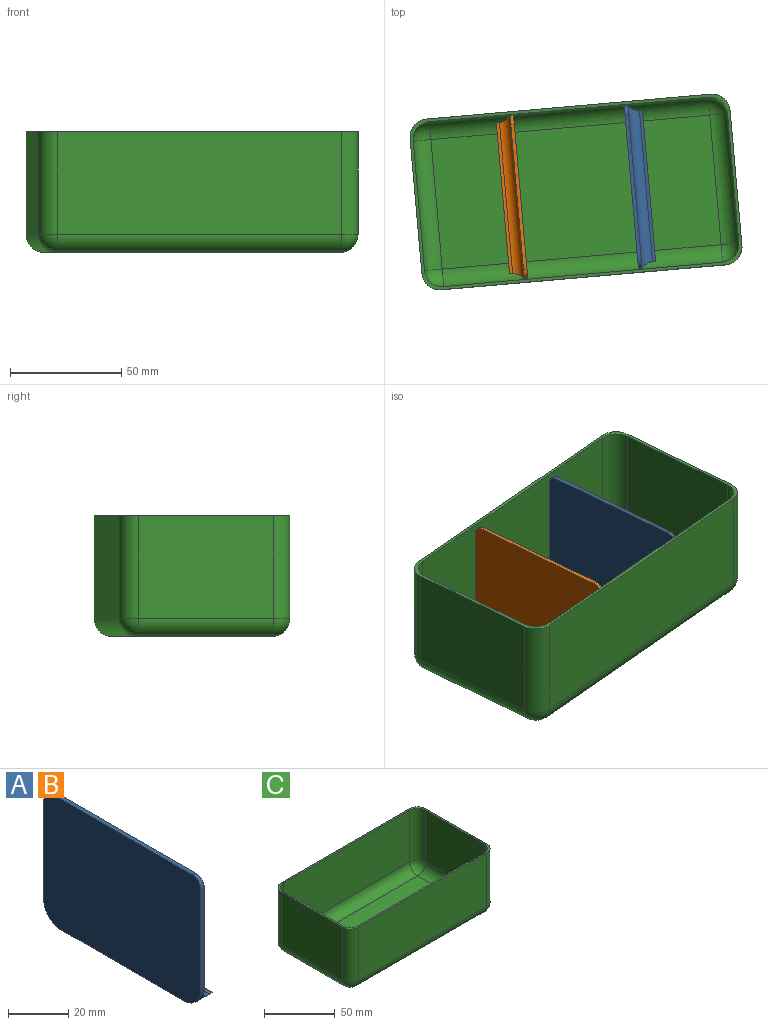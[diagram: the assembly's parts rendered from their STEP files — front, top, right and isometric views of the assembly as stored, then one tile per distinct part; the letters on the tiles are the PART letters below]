
ASSEMBLY  parts=3 mates=2
PART A: 13 faces, bbox 8x73.6x53 mm
  f0: plane 57.6x8mm, normal (0,0,-1), area 460.8mm2, adj f1,f5,f8,f9
  f1: plane 68.18x2mm, normal (1,0,0), area 129.7mm2, adj f0,f2,f8,f9
  f2: plane 68.18x1.4mm, normal (0,0,1), area 95.5mm2, adj f1,f8,f9,f10
  f3: plane 73.6x46mm, normal (1,0,0), area 3378.7mm2, adj f4,f6,f7,f8,f9,f10,f11,f12
  f4: plane 65.6x1.6mm, normal (0,0,1), area 105mm2, adj f3,f5,f11,f12
  f5: plane 73.6x53mm, normal (-1,0,0), area 3866.5mm2, adj f0,f4,f6,f7,f8,f9,f11,f12
  f6: plane 41x1.6mm, normal (0,-1,0), area 65.6mm2, adj f3,f5,f9,f12
  f7: plane 41x1.6mm, normal (0,1,0), area 65.6mm2, adj f3,f5,f8,f11
  f8: cylinder r=8mm len=8mm, axis (1,0,0), area 64.1mm2, adj f0,f1,f2,f3,f5,f7,f10
  f9: cylinder r=8mm len=8mm, axis (-1,0,0), area 64.1mm2, adj f0,f1,f2,f3,f5,f6,f10
  f10: cylinder r=5mm len=73.47mm, axis (0,1,0), area 555.8mm2, adj f2,f3,f8,f9
  f11: cylinder r=4mm len=4mm, axis (-1,0,0), area 10.1mm2, adj f3,f4,f5,f7
  f12: cylinder r=4mm len=4mm, axis (1,0,0), area 10.1mm2, adj f3,f4,f5,f6
PART B: same geometry as A
PART C: 35 faces, bbox 144.6x77.1x54.3 mm
  f0: plane 61.1x46.3mm, normal (1,0,0), area 2828.9mm2, adj f8,f13,f16,f26
  f1: plane 128.6x46.3mm, normal (0,1,0), area 5954.2mm2, adj f8,f13,f14,f22
  f2: plane 61.1x46.3mm, normal (-1,0,0), area 2828.9mm2, adj f8,f14,f15,f19
  f3: plane 58.5x45mm, normal (1,0,0), area 2632.5mm2, adj f8,f9,f12,f32
  f4: plane 126x45mm, normal (0,-1,0), area 5670mm2, adj f8,f9,f10,f28
  f5: plane 58.5x45mm, normal (-1,0,0), area 2632.5mm2, adj f8,f10,f11,f29
  f6: plane 126x45mm, normal (0,1,0), area 5670mm2, adj f8,f11,f12,f33
  f7: plane 128.6x46.3mm, normal (0,-1,0), area 5954.2mm2, adj f8,f15,f16,f23
  f8: plane 144.6x77.1mm, normal (0,0,1), area 569.7mm2, adj f0,f1,f2,f3,f4,f5,f6,f7
  f9: cylinder r=8mm len=45mm, axis (0,0,-1), area 565.5mm2, adj f3,f4,f8,f30
  f10: cylinder r=8mm len=45mm, axis (0,0,1), area 565.5mm2, adj f4,f5,f8,f27
  f11: cylinder r=8mm len=45mm, axis (0,0,-1), area 565.5mm2, adj f5,f6,f8,f31
  f12: cylinder r=8mm len=45mm, axis (0,0,1), area 565.5mm2, adj f3,f6,f8,f34
  f13: cylinder r=8mm len=46.3mm, axis (0,0,-1), area 581.8mm2, adj f0,f1,f8,f24
  f14: cylinder r=8mm len=46.3mm, axis (0,0,1), area 581.8mm2, adj f1,f2,f8,f20
  f15: cylinder r=8mm len=46.3mm, axis (0,0,-1), area 581.8mm2, adj f2,f7,f8,f21
  f16: cylinder r=8mm len=46.3mm, axis (0,0,1), area 581.8mm2, adj f0,f7,f8,f25
  f17: plane 126x58.5mm, normal (0,0,1), area 7371mm2, adj f28,f29,f32,f33
  f18: plane 128.6x61.1mm, normal (0,0,-1), area 7857.5mm2, adj f19,f22,f23,f26
  f19: cylinder r=8mm len=61.1mm, axis (0,-1,0), area 767.8mm2, adj f2,f18,f20,f21
  f20: sphere r=8mm, area 100.5mm2, adj f14,f19,f22
  f21: sphere r=8mm, area 100.5mm2, adj f15,f19,f23
  f22: cylinder r=8mm len=128.6mm, axis (-1,0,0), area 1616mm2, adj f1,f18,f20,f24
  f23: cylinder r=8mm len=128.6mm, axis (1,0,0), area 1616mm2, adj f7,f18,f21,f25
  f24: sphere r=8mm, area 100.5mm2, adj f13,f22,f26
  f25: sphere r=8mm, area 100.5mm2, adj f16,f23,f26
  f26: cylinder r=8mm len=61.1mm, axis (0,1,0), area 767.8mm2, adj f0,f18,f24,f25
  f27: sphere r=8mm, area 100.5mm2, adj f10,f28,f29
  f28: cylinder r=8mm len=126mm, axis (1,0,0), area 1583.4mm2, adj f4,f17,f27,f30
  f29: cylinder r=8mm len=58.5mm, axis (0,-1,0), area 735.1mm2, adj f5,f17,f27,f31
  f30: sphere r=8mm, area 100.5mm2, adj f9,f28,f32
  f31: sphere r=8mm, area 100.5mm2, adj f11,f29,f33
  f32: cylinder r=8mm len=58.5mm, axis (0,1,0), area 735.1mm2, adj f3,f17,f30,f34
  f33: cylinder r=8mm len=126mm, axis (-1,0,0), area 1583.4mm2, adj f6,f17,f31,f34
  f34: sphere r=8mm, area 100.5mm2, adj f12,f32,f33
PLACE A rot(axis=(0,0,1),5deg) t=(24.05,6.91,-15.91)mm
PLACE B rot(axis=(0,0,-1),175deg) t=(-25.76,2.55,-15.91)mm
PLACE C rot(axis=(0,0,1),5deg) t=(-0.85,4.73,-15.91)mm
MATE revolute B.f0 <-> C.f17  axis (0,0,1) through (-25.76,2.55,-15.91)mm
MATE fastened A.f0 <-> C.f17  axis (0,0,1) through (24.05,6.91,-15.91)mm
